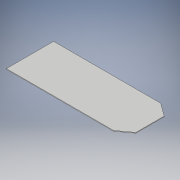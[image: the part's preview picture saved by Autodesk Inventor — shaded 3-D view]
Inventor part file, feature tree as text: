
AUTODESK INVENTOR PART (.ipt)
format: ipt  version: 2018 (Build 220112000, 112)  size: 95,232 bytes
history: native  units: in
note: dims shown in document units (in); Inventor stores cm internally (conversion verified against a paired STEP export)
features: extrude x1, sketch x1
ambient origin geometry x8: Origin, YZ Plane, XZ Plane, XY Plane, X Axis, Y Axis, Z Axis, Center Point
bodies: Solid1 (feature_tree)
feature tree (2):
  extrude  "Extrusion1"  Depth=2.1654in
  sketch  "Sketch1"  dims[d0=4.9213in d1=2.1654in d2=1.2992in d3=90.0deg d4=0.031in d5=0.0in]
